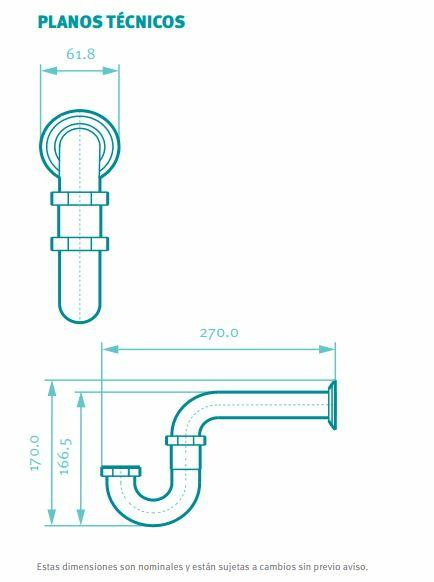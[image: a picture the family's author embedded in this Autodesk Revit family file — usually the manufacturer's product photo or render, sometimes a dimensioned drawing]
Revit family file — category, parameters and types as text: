
# Revit family: 935080001_Sifon en P
name_source: partatom
category: Plumbing Fixtures
units: mm (PartAtom-declared; Revit-internal decimal feet)

## family parameters
Always vertical = Yes
Cut with Voids When Loaded = No
Host = Wall
OmniClass Number = 23.27.43.00
OmniClass Title = Pipe Fittings
Part Type = Normal
Room Calculation Point = No
Round Connector Dimension = Use Diameter
Shared = No

## types (1)
- Type 1
    Alto = 170 mm  [stored 0.557743 ft]
    Ancho = 62 mm
    Creado por = BIMBAU
    Default Elevation = 0 mm  [stored 0 ft]
    Description = Para uso en lavamanos o lavaplatos. Trampa que retiene olores y residuos.
    Fabricante = Grival
    Fecha de creación = 7/04/2020
    Garantía = 30 años
    Material = Corona_Plastico_Gris
    Profundidad = 270 mm  [stored 0.885827 ft]
    Referencia = 935080001
    Resistencia = Resistente a la corrosión
pelado y decoloración por agua.
    URL = https://corona.co
    Uso = Residencial
    Ventajas = Elaborado en resina de alta ingeniería. Fácil instalación, limpieza y mantenimiento. Cuerpo plástico Elaborado en resina de alta ingeniería,
soporta altas presiones y temperatura elevadas.

note: [stored X ft] marks values corroborated as IEEE doubles in the binary element streams (Revit-internal decimal feet)

## geometry (parser evidence)
native form markers: Sweep x4
no freeform markers — native parametric forms only
